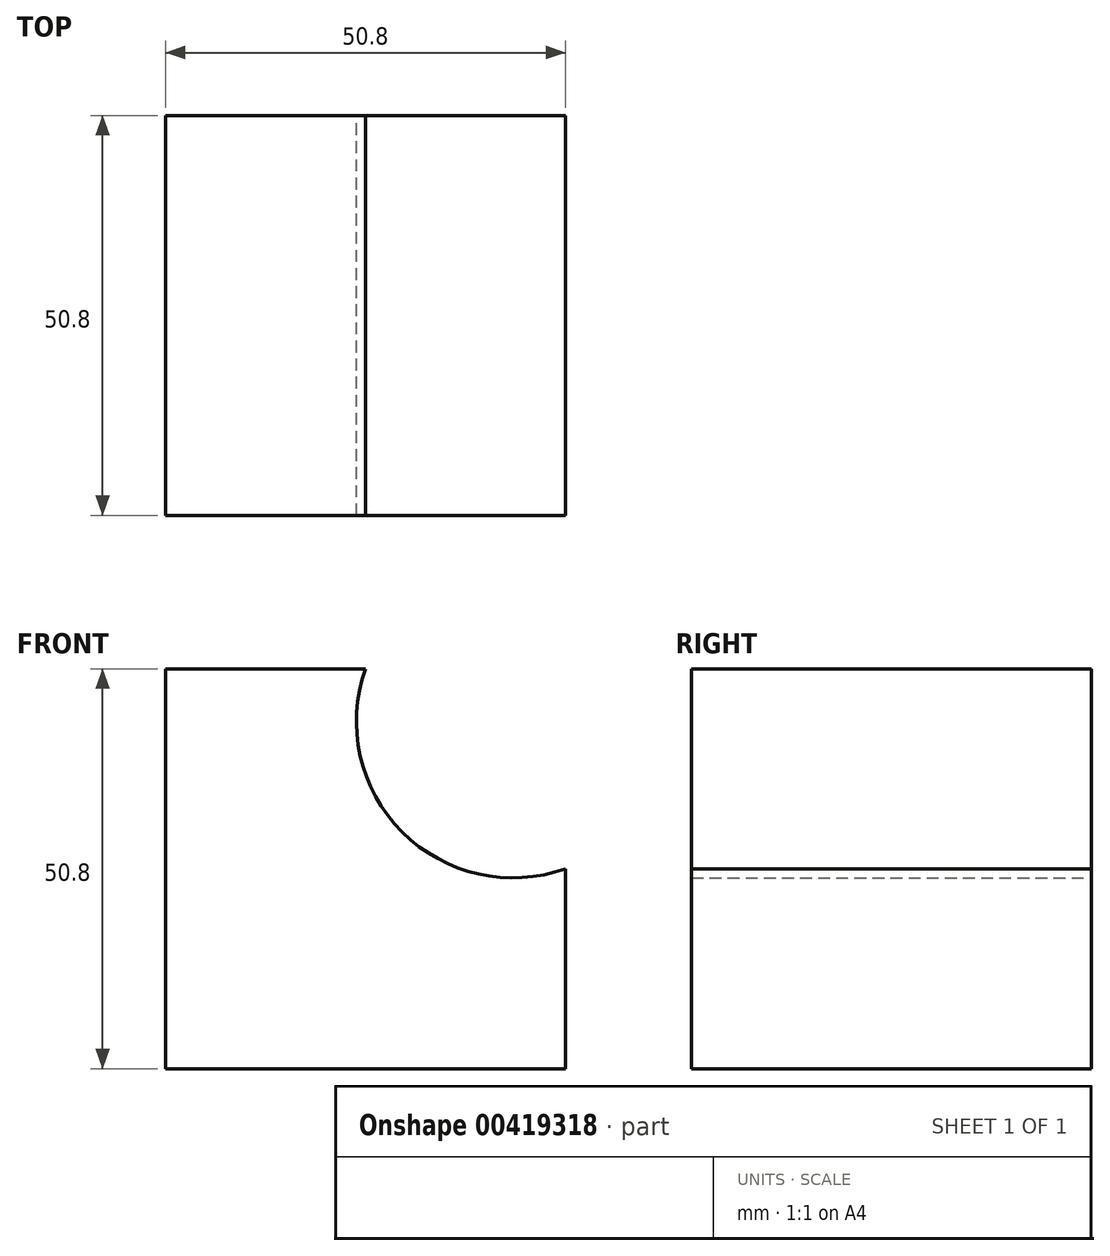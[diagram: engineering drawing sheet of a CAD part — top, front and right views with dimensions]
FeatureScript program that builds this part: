
annotation { "Feature Type Name" : "Feature", "Feature Type Description" : "" }
export const myFeature = defineFeature(function(context is Context, id is Id, definition is map)
    precondition{}
    {
        {
            var Q0;
            Q0=qCreatedBy(makeId("Front.planeOp"),FACE);
            var sketch = newSketch(context, id + "F0", { "sketchPlane" : qUnion([Q0])});
            skLineSegment(sketch, "E0", {"start": v(0, 0) * mm, "end": v(-50.8, 0) * mm});
            skLineSegment(sketch, "E1", {"start": v(-50.8, 0) * mm, "end": v(-50.8, 50.8) * mm});
            skLineSegment(sketch, "E2", {"start": v(-50.8, 50.8) * mm, "end": v(-25.4, 50.8) * mm});
            skLineSegment(sketch, "E3", {"start": v(0, 0) * mm, "end": v(0, 25.4) * mm});
            skArc(sketch, "E4", {"start": v(-25.4, 50.8) * mm, "mid": v(-20.74, 30.06) * mm, "end": v(0, 25.4) * mm});
            skSolve(sketch);
        }
        {
            var Q0;
            Q0=makeQuery(id+"F0.imprint","IMPRINT",FACE,{"disambiguationData":[TD([[makeQuery(id+"F0.imprint","IMPRINT",EDGE,{"derivedFrom":sQuery(id+"F0.wireOp",EDGE,"E0")}),-1.0]])]});
            extrude(context, id + "F1", {"entities" : qUnion([Q0]), "depth" : 50.8 * mm});
        }
    });
